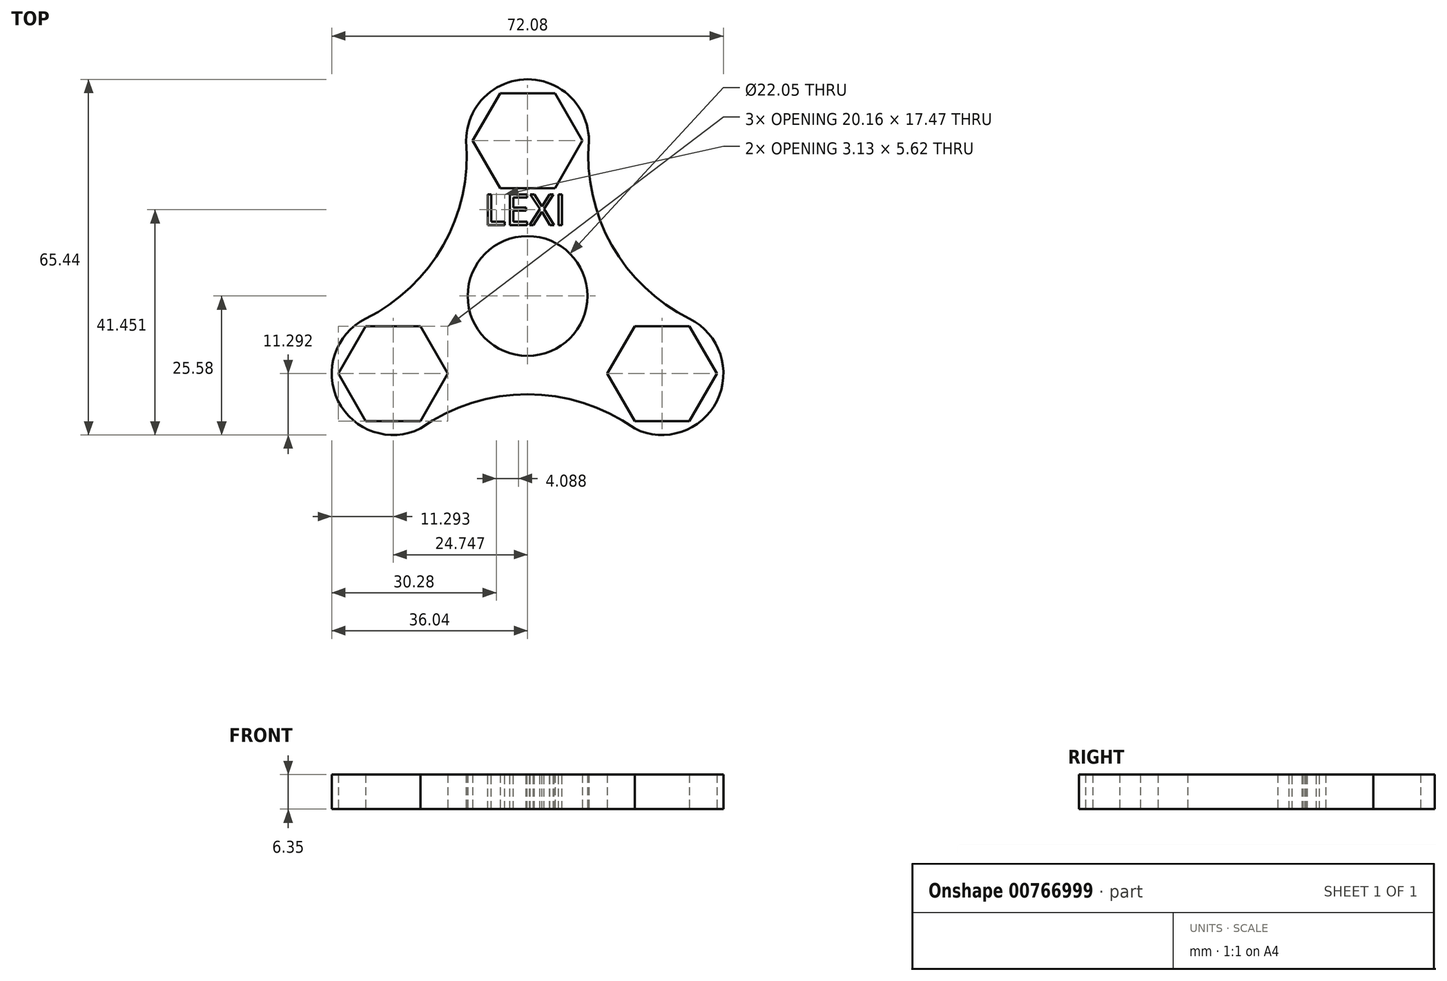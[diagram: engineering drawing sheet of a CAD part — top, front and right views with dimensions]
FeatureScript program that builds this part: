
annotation { "Feature Type Name" : "Feature", "Feature Type Description" : "" }
export const myFeature = defineFeature(function(context is Context, id is Id, definition is map)
    precondition{}
    {
        {
            var Q0;
            Q0=qCreatedBy(makeId("Top.planeOp"),FACE);
            var sketch = newSketch(context, id + "F0", { "sketchPlane" : qUnion([Q0])});
            skCircle(sketch, "E0", {"center": v(0, 0) * mm, "radius": 11.02 * mm});
            skCircle(sketch, "E1", {"center": v(0, 0) * mm, "radius": 14.29 * mm});
            skCircle(sketch, "E2.cCircle", {"center": v(0, 28.58) * mm, "radius": 8.73 * mm, "construction": true});
            skLineSegment(sketch, "E2.0", {"start": v(10.08, 28.57) * mm, "end": v(5.04, 19.84) * mm});
            skLineSegment(sketch, "E2.1", {"start": v(5.04, 19.84) * mm, "end": v(-5.04, 19.85) * mm});
            skLineSegment(sketch, "E2.2", {"start": v(-5.04, 19.85) * mm, "end": v(-10.08, 28.58) * mm});
            skLineSegment(sketch, "E2.3", {"start": v(-10.08, 28.58) * mm, "end": v(-5.04, 37.3) * mm});
            skLineSegment(sketch, "E2.4", {"start": v(-5.04, 37.3) * mm, "end": v(5.04, 37.3) * mm});
            skLineSegment(sketch, "E2.5", {"start": v(5.04, 37.3) * mm, "end": v(10.08, 28.57) * mm});
            skPoint(sketch, "E2.0.midPoint", {"position": v(7.56, 24.2) * mm});
            skCircle(sketch, "E3", {"center": v(0, 28.58) * mm, "radius": 11.29 * mm});
            skLineSegment(sketch, "E4.1.0", {"start": v(-19.7, -23.02) * mm, "end": v(-29.8, -23.02) * mm});
            skCircle(sketch, "E4.1.1", {"center": v(-24.75, -14.29) * mm, "radius": 11.29 * mm});
            skPoint(sketch, "E4.1.2", {"position": v(-24.74, -5.56) * mm});
            skCircle(sketch, "E4.1.3", {"center": v(-24.75, -14.29) * mm, "radius": 8.73 * mm, "construction": true});
            skLineSegment(sketch, "E4.1.4", {"start": v(-34.83, -14.28) * mm, "end": v(-29.78, -5.55) * mm});
            skLineSegment(sketch, "E4.1.5", {"start": v(-29.8, -23.02) * mm, "end": v(-34.83, -14.28) * mm});
            skLineSegment(sketch, "E4.1.6", {"start": v(-14.66, -14.3) * mm, "end": v(-19.7, -23.02) * mm});
            skLineSegment(sketch, "E4.1.7", {"start": v(-19.7, -5.56) * mm, "end": v(-14.66, -14.3) * mm});
            skLineSegment(sketch, "E4.1.8", {"start": v(-29.78, -5.55) * mm, "end": v(-19.7, -5.56) * mm});
            skLineSegment(sketch, "E4.2.0", {"start": v(29.8, -5.56) * mm, "end": v(34.83, -14.3) * mm});
            skCircle(sketch, "E4.2.1", {"center": v(24.75, -14.29) * mm, "radius": 11.29 * mm});
            skPoint(sketch, "E4.2.2", {"position": v(17.18, -18.65) * mm});
            skCircle(sketch, "E4.2.3", {"center": v(24.75, -14.29) * mm, "radius": 8.73 * mm, "construction": true});
            skLineSegment(sketch, "E4.2.4", {"start": v(29.78, -23.02) * mm, "end": v(19.7, -23.02) * mm});
            skLineSegment(sketch, "E4.2.5", {"start": v(34.83, -14.3) * mm, "end": v(29.78, -23.02) * mm});
            skLineSegment(sketch, "E4.2.6", {"start": v(19.7, -5.55) * mm, "end": v(29.8, -5.56) * mm});
            skLineSegment(sketch, "E4.2.7", {"start": v(14.66, -14.28) * mm, "end": v(19.7, -5.55) * mm});
            skLineSegment(sketch, "E4.2.8", {"start": v(19.7, -23.02) * mm, "end": v(14.66, -14.28) * mm});
            skArc(sketch, "E5", {"start": v(-29.78, -4.19) * mm, "mid": v(-15.5, 9.35) * mm, "end": v(-11.29, 28.58) * mm});
            skArc(sketch, "E6", {"start": v(11.29, 28.57) * mm, "mid": v(15.5, 9.35) * mm, "end": v(29.8, -4.19) * mm});
            skArc(sketch, "E7", {"start": v(19.7, -24.39) * mm, "mid": v(0, -18.1) * mm, "end": v(-19.7, -24.39) * mm});
            skSolve(sketch);
        }
        {
            var Q0;
            Q0=makeQuery(id+"F0.imprint","IMPRINT",FACE,{"disambiguationData":[TD([[makeQuery(id+"F0.imprint","IMPRINT",EDGE,{"derivedFrom":sQuery(id+"F0.wireOp",EDGE,"E1")}),-1.0]])]});
            var Q1;
            Q1=makeQuery(id+"F0.imprint","IMPRINT",FACE,{"disambiguationData":[TD([[makeQuery(id+"F0.imprint","IMPRINT",EDGE,{"derivedFrom":sQuery(id+"F0.wireOp",EDGE,"E0")}),-1.0]])]});
            var Q2;
            Q2=makeQuery(id+"F0.imprint","IMPRINT",FACE,{"disambiguationData":[TD([[makeQuery(id+"F0.imprint","IMPRINT",EDGE,{"derivedFrom":sQuery(id+"F0.wireOp",EDGE,"E2.0")}),1.0]])]});
            var Q3;
            Q3=makeQuery(id+"F0.imprint","IMPRINT",FACE,{"disambiguationData":[TD([[makeQuery(id+"F0.imprint","IMPRINT",EDGE,{"derivedFrom":sQuery(id+"F0.wireOp",EDGE,"E4.2.0")}),1.0]])]});
            var Q4;
            Q4=makeQuery(id+"F0.imprint","IMPRINT",FACE,{"disambiguationData":[TD([[makeQuery(id+"F0.imprint","IMPRINT",EDGE,{"derivedFrom":sQuery(id+"F0.wireOp",EDGE,"E4.1.0")}),1.0]])]});
            extrude(context, id + "F1", {"entities" : qUnion([Q0, Q1, Q2, Q3, Q4]), "depth" : 6.35 * mm, "offsetDistance" : 25.4 * mm});
        }
        {
            var Q0;
            Q0=makeQuery(id+"F1.opExtrude","CAP_FACE",FACE,{"disambiguationData":[OSD([sQuery(id+"F0.wireOp",EDGE,"E0"),sQuery(id+"F0.wireOp",EDGE,"E2.0"),sQuery(id+"F0.wireOp",EDGE,"E2.1"),sQuery(id+"F0.wireOp",EDGE,"E2.2"),sQuery(id+"F0.wireOp",EDGE,"E2.3"),sQuery(id+"F0.wireOp",EDGE,"E2.4"),sQuery(id+"F0.wireOp",EDGE,"E2.5"),sQuery(id+"F0.wireOp",EDGE,"E3"),sQuery(id+"F0.wireOp",EDGE,"E4.1.0"),sQuery(id+"F0.wireOp",EDGE,"E4.1.1"),sQuery(id+"F0.wireOp",EDGE,"E4.1.4"),sQuery(id+"F0.wireOp",EDGE,"E4.1.5"),sQuery(id+"F0.wireOp",EDGE,"E4.1.6"),sQuery(id+"F0.wireOp",EDGE,"E4.1.7"),sQuery(id+"F0.wireOp",EDGE,"E4.1.8"),sQuery(id+"F0.wireOp",EDGE,"E4.2.0"),sQuery(id+"F0.wireOp",EDGE,"E4.2.1"),sQuery(id+"F0.wireOp",EDGE,"E4.2.4"),sQuery(id+"F0.wireOp",EDGE,"E4.2.5"),sQuery(id+"F0.wireOp",EDGE,"E4.2.6"),sQuery(id+"F0.wireOp",EDGE,"E4.2.7"),sQuery(id+"F0.wireOp",EDGE,"E4.2.8"),sQuery(id+"F0.wireOp",EDGE,"E5"),sQuery(id+"F0.wireOp",EDGE,"E6"),sQuery(id+"F0.wireOp",EDGE,"E7")])],"isStart":false});
            var sketch = newSketch(context, id + "F2", { "sketchPlane" : qUnion([Q0])});
            skText(sketch, "E8", { "text": "LEXI", "fontName": "OpenSans-Regular.ttf"});
            const initialGuessF2  = {"E8": [-0.0081, 0.01306, 1, 0, 0.00567]};
            skSetInitialGuess(sketch, initialGuessF2);
            skSolve(sketch);
        }
        {
            var Q0;
            Q0 = qSketchRegion(id + "F2", true);
            extrude(context, id + "F3", {"entities" : qUnion([Q0]), "operationType" : NewBodyOperationType.REMOVE, "oppositeDirection" : true, "depth" : 25.4 * mm, "offsetDistance" : 25.4 * mm});
        }
    });
